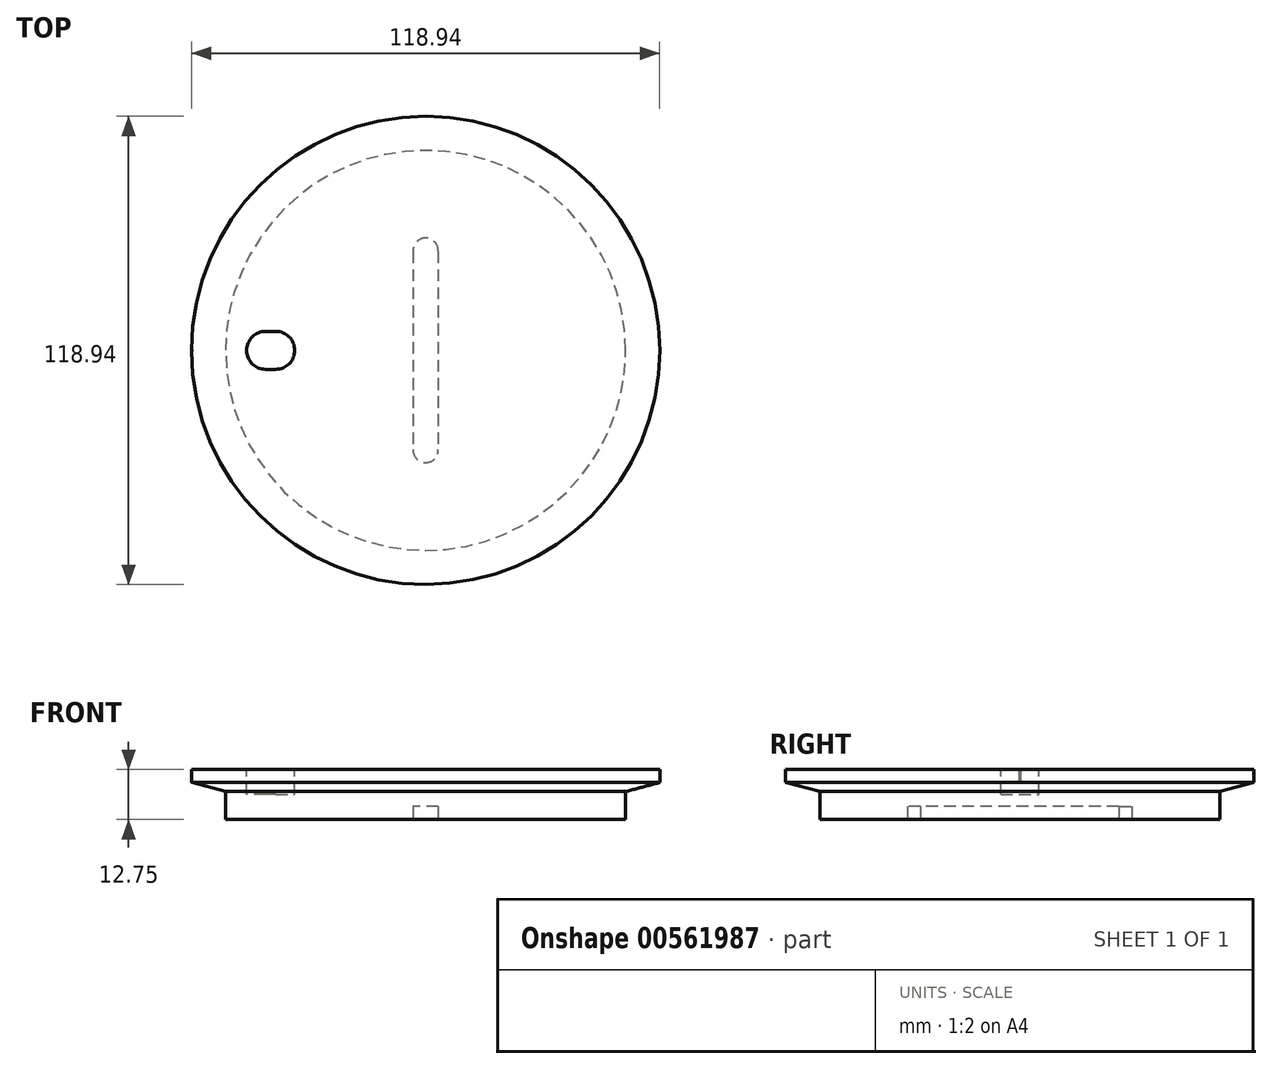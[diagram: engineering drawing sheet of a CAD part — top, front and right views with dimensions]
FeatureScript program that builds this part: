
annotation { "Feature Type Name" : "Feature", "Feature Type Description" : "" }
export const myFeature = defineFeature(function(context is Context, id is Id, definition is map)
    precondition{}
    {
        {
            var Q0;
            Q0=qCreatedBy(makeId("Front.planeOp"),FACE);
            var sketch = newSketch(context, id + "F0", { "sketchPlane" : qUnion([Q0])});
            skLineSegment(sketch, "E0", {"start": v(0, 0) * mm, "end": v(0, 85.37) * mm, "construction": true});
            skLineSegment(sketch, "E1", {"start": v(0, 0) * mm, "end": v(0, -83.14) * mm, "construction": true});
            skLineSegment(sketch, "E2", {"start": v(0, 0) * mm, "end": v(59.47, 0) * mm});
            skLineSegment(sketch, "E3", {"start": v(59.47, 0) * mm, "end": v(59.47, -3.3) * mm});
            skLineSegment(sketch, "E4", {"start": v(59.47, -3.3) * mm, "end": v(50.8, -5.63) * mm});
            skLineSegment(sketch, "E5", {"start": v(0, 0) * mm, "end": v(0, -12.75) * mm});
            skLineSegment(sketch, "E6", {"start": v(0, -12.75) * mm, "end": v(50.8, -12.75) * mm});
            skLineSegment(sketch, "E7", {"start": v(50.8, -12.75) * mm, "end": v(50.8, -5.63) * mm});
            skSolve(sketch);
        }
        {
            var Q0;
            Q0=makeQuery(id+"F0.imprint","IMPRINT",FACE,{"disambiguationData":[TD([[makeQuery(id+"F0.imprint","IMPRINT",EDGE,{"derivedFrom":sQuery(id+"F0.wireOp",EDGE,"E2")}),-1.0]])]});
            var Q1;
            Q1=sQuery(id+"F0.wireOp",EDGE,"E5");
            revolve(context, id + "F1", {"entities" : qUnion([Q0]), "axis" : qUnion([Q1]), "revolveType" : RevolveType.FULL});
        }
        {
            var Q0;
            Q0=makeQuery(id+"F1.opRevolve","SWEPT_FACE",FACE,{"disambiguationData":[OSD([sQuery(id+"F0.wireOp",EDGE,"E2")])]});
            var sketch = newSketch(context, id + "F2", { "sketchPlane" : qUnion([Q0])});
            skLineSegment(sketch, "E8", {"start": v(-38.1, -4.83) * mm, "end": v(-40.64, -4.83) * mm});
            skLineSegment(sketch, "E9", {"start": v(-40.64, 4.83) * mm, "end": v(-38.1, 4.83) * mm});
            skArc(sketch, "E10", {"start": v(-38.1, -4.83) * mm, "mid": v(-33.27, 0) * mm, "end": v(-38.1, 4.83) * mm});
            skArc(sketch, "E11", {"start": v(-40.64, 4.83) * mm, "mid": v(-45.47, 0) * mm, "end": v(-40.64, -4.83) * mm});
            skPoint(sketch, "E12.orphan", {"position": v(-38.1, 4.83) * mm});
            skPoint(sketch, "E13.orphan", {"position": v(-38.1, -4.83) * mm});
            skPoint(sketch, "E14.start.orphan", {"position": v(0, 4.83) * mm});
            skSolve(sketch);
        }
        {
            var Q0;
            Q0=qSketchRegion(id+"F2",true);
            extrude(context, id + "F3", {"entities" : qUnion([Q0]), "operationType" : NewBodyOperationType.REMOVE, "oppositeDirection" : true, "depth" : 6.35 * mm, "offsetDistance" : 25.4 * mm});
        }
        {
            var Q0;
            Q0=makeQuery(id+"F1.opRevolve","SWEPT_FACE",FACE,{"disambiguationData":[OSD([sQuery(id+"F0.wireOp",EDGE,"E2")])]});
            var sketch = newSketch(context, id + "F4", { "sketchPlane" : qUnion([Q0])});
            skLineSegment(sketch, "E15.0", {"start": v(-59.35, 0.13) * mm, "end": v(-59.47, 0.13) * mm});
            skLineSegment(sketch, "E16.0", {"start": v(-59.35, -0.13) * mm, "end": v(-59.47, -0.13) * mm});
            skArc(sketch, "E17.0", {"start": v(-59.35, 0.13) * mm, "mid": v(-59.35, 0) * mm, "end": v(-59.35, -0.13) * mm});
            skLineSegment(sketch, "E18", {"start": v(-59.47, -0.13) * mm, "end": v(-59.47, 0.13) * mm});
            skPoint(sketch, "E19.start.orphan", {"position": v(-40.64, 0) * mm});
            skSolve(sketch);
        }
        {
            var Q0;
            Q0=qSketchRegion(id+"F4",true);
            extrude(context, id + "F5", {"entities" : qUnion([Q0]), "operationType" : NewBodyOperationType.REMOVE, "oppositeDirection" : true, "depth" : 25.4 * mm, "offsetDistance" : 25.4 * mm});
        }
        {
            var Q0;
            Q0=makeQuery(id+"F1.opRevolve","SWEPT_FACE",FACE,{"disambiguationData":[OSD([sQuery(id+"F0.wireOp",EDGE,"E6")])]});
            var sketch = newSketch(context, id + "F6", { "sketchPlane" : qUnion([Q0])});
            skLineSegment(sketch, "E20.0", {"start": v(3.17, 0) * mm, "end": v(3.17, 25.36) * mm});
            skLineSegment(sketch, "E21.0", {"start": v(-3.17, 0) * mm, "end": v(-3.17, 25.36) * mm});
            skLineSegment(sketch, "E22.0", {"start": v(-3.17, 0) * mm, "end": v(-3.17, -25.36) * mm});
            skLineSegment(sketch, "E23.0", {"start": v(3.17, 0) * mm, "end": v(3.17, -25.36) * mm});
            skArc(sketch, "E24", {"start": v(3.17, 25.17) * mm, "mid": v(0, 28.53) * mm, "end": v(-3.17, 25.17) * mm});
            skArc(sketch, "E25", {"start": v(-3.17, -25.17) * mm, "mid": v(0, -28.53) * mm, "end": v(3.17, -25.17) * mm});
            skSolve(sketch);
        }
        {
            var Q0;
            Q0=makeQuery(id+"F6.imprint","IMPRINT",FACE,{"disambiguationData":[TD([[makeQuery(id+"F6.imprint","IMPRINT",EDGE,{"derivedFrom":sQuery(id+"F6.wireOp",EDGE,"E20.0")}),1.0]])]});
            extrude(context, id + "F7", {"entities" : qUnion([Q0]), "operationType" : NewBodyOperationType.REMOVE, "oppositeDirection" : true, "depth" : 3.17 * mm, "offsetDistance" : 25.4 * mm});
        }
        {
            var Q0;
            Q0 = qSketchRegion(id + "F6", true);
            extrude(context, id + "F8", {"entities" : qUnion([Q0]), "operationType" : NewBodyOperationType.REMOVE, "oppositeDirection" : true, "depth" : 3.3 * mm, "offsetDistance" : 25.4 * mm});
        }
    });
